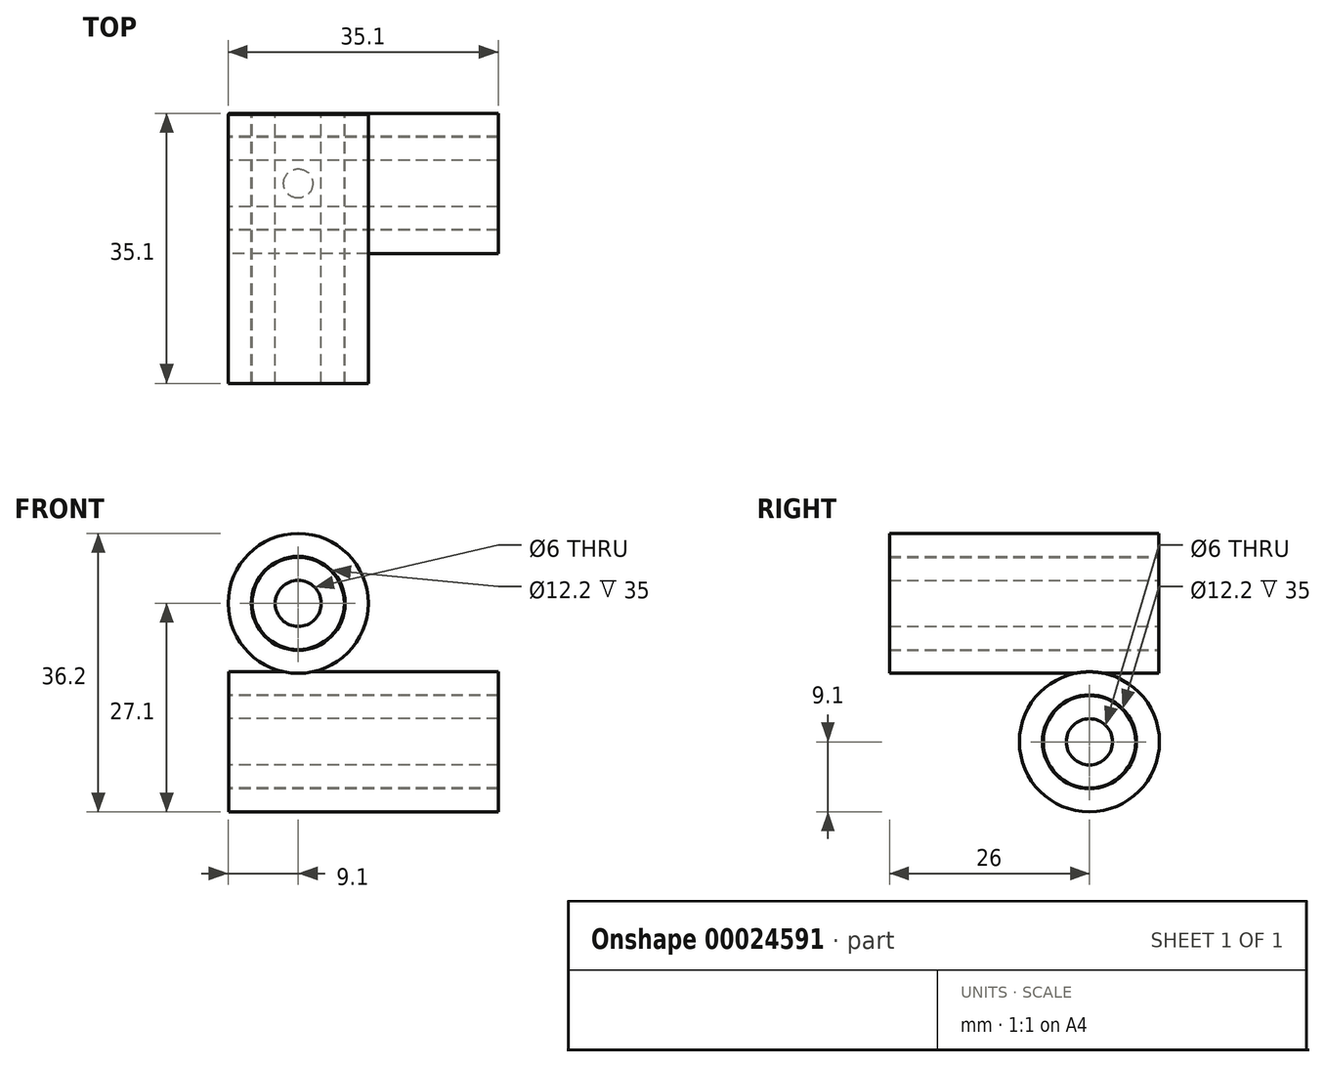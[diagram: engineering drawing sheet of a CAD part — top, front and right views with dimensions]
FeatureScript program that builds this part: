
annotation { "Feature Type Name" : "Feature", "Feature Type Description" : "" }
export const myFeature = defineFeature(function(context is Context, id is Id, definition is map)
    precondition{}
    {
        {
            assignVariable(context, id + "F0", {"name" : "lm6uu_l", "anyValue" : 35});
        }
        {
            var Q0;
            Q0=qCreatedBy(makeId("Front.planeOp"),FACE);
            cPlane(context, id + "F1", {"entities" : qUnion([Q0]), "cplaneType" : CPlaneType.OFFSET, "offset" : 9 * mm, "oppositeDirection" : true, "width" : 150 * mm, "height" : 150 * mm});
        }
        {
            var Q0;
            Q0=qCreatedBy(id+"F1.planeOp",FACE);
            var sketch = newSketch(context, id + "F2", { "sketchPlane" : qUnion([Q0])});
            skCircle(sketch, "E0", {"center": v(0, 50) * mm, "radius": 6 * mm});
            skCircle(sketch, "E1", {"center": v(0, 50) * mm, "radius": 3 * mm});
            skSolve(sketch);
        }
        {
            var Q0;
            Q0=makeQuery(id+"F2.imprint","IMPRINT",FACE,{"disambiguationData":[TD([[makeQuery(id+"F2.imprint","IMPRINT",EDGE,{"derivedFrom":sQuery(id+"F2.wireOp",EDGE,"E0")}),1.0]])]});
            extrude(context, id + "F3", {"entities" : qUnion([Q0]), "depth" : (getVariable(context, 'lm6uu_l')) * mm});
        }
        {
            var Q0;
            Q0=qCreatedBy(makeId("Right.planeOp"),FACE);
            cPlane(context, id + "F4", {"entities" : qUnion([Q0]), "cplaneType" : CPlaneType.OFFSET, "offset" : 9 * mm, "oppositeDirection" : true, "width" : 150 * mm, "height" : 150 * mm});
        }
        {
            var Q0;
            Q0=qCreatedBy(id+"F4.planeOp",FACE);
            var sketch = newSketch(context, id + "F5", { "sketchPlane" : qUnion([Q0])});
            skLineSegment(sketch, "E2", {"start": v(-35, 56) * mm, "end": v(0, 56) * mm, "construction": true});
            skLineSegment(sketch, "E3", {"start": v(0, 44) * mm, "end": v(-35, 44) * mm, "construction": true});
            skLineSegment(sketch, "E4", {"start": v(-47.11, 50) * mm, "end": v(12.64, 50) * mm, "construction": true});
            skCircle(sketch, "E5", {"center": v(0, 32) * mm, "radius": 6 * mm});
            skCircle(sketch, "E6", {"center": v(0, 32) * mm, "radius": 3 * mm});
            skSolve(sketch);
        }
        {
            var Q0;
            Q0=makeQuery(id+"F5.imprint","IMPRINT",FACE,{"disambiguationData":[TD([[makeQuery(id+"F5.imprint","IMPRINT",EDGE,{"derivedFrom":sQuery(id+"F5.wireOp",EDGE,"E5")}),1.0]])]});
            extrude(context, id + "F6", {"entities" : qUnion([Q0]), "depth" : (getVariable(context, 'lm6uu_l')) * mm});
        }
        {
            var Q0;
            Q0=qCreatedBy(id+"F1.planeOp",FACE);
            var sketch = newSketch(context, id + "F7", { "sketchPlane" : qUnion([Q0])});
            skCircle(sketch, "E7.0", {"center": v(0, 50) * mm, "radius": 3 * mm, "construction": true});
            skCircle(sketch, "E8.0", {"center": v(0, 50) * mm, "radius": 6 * mm, "construction": true});
            skCircle(sketch, "E9.0", {"center": v(0, 50) * mm, "radius": 6.1 * mm});
            skCircle(sketch, "E10.0", {"center": v(0, 50) * mm, "radius": 9.1 * mm});
            skSolve(sketch);
        }
        {
            var Q0;
            Q0 = qSketchRegion(id + "F7", true);
            extrude(context, id + "F8", {"entities" : qUnion([Q0]), "depth" : (getVariable(context, 'lm6uu_l')) * mm});
        }
        {
            var Q0;
            Q0=qCreatedBy(id+"F4.planeOp",FACE);
            var sketch = newSketch(context, id + "F9", { "sketchPlane" : qUnion([Q0])});
            skCircle(sketch, "E11.0", {"center": v(0, 32) * mm, "radius": 6 * mm});
            skCircle(sketch, "E12.0", {"center": v(0, 32) * mm, "radius": 6.1 * mm});
            skCircle(sketch, "E13.0", {"center": v(0, 32) * mm, "radius": 9.1 * mm});
            skLineSegment(sketch, "E14", {"start": v(-15.96, 32) * mm, "end": v(16.3, 32) * mm, "construction": true});
            skLineSegment(sketch, "E15", {"start": v(-9.1, 32) * mm, "end": v(-9.1, 41.1) * mm});
            skLineSegment(sketch, "E16", {"start": v(-9.1, 41.1) * mm, "end": v(0, 41.1) * mm});
            skLineSegment(sketch, "E17", {"start": v(0, 41.1) * mm, "end": v(9.1, 41.1) * mm});
            skLineSegment(sketch, "E18", {"start": v(9.1, 41.1) * mm, "end": v(9.1, 32) * mm});
            skSolve(sketch);
        }
        {
            var Q0;
            Q0=makeQuery(id+"F9.imprint","IMPRINT",FACE,{"disambiguationData":[TD([[makeQuery(id+"F9.imprint","IMPRINT",EDGE,{"derivedFrom":sQuery(id+"F9.wireOp",EDGE,"E12.0")}),-1.0]])]});
            extrude(context, id + "F10", {"entities" : qUnion([Q0]), "operationType" : NewBodyOperationType.ADD, "depth" : (getVariable(context, 'lm6uu_l')) * mm});
        }
    });
